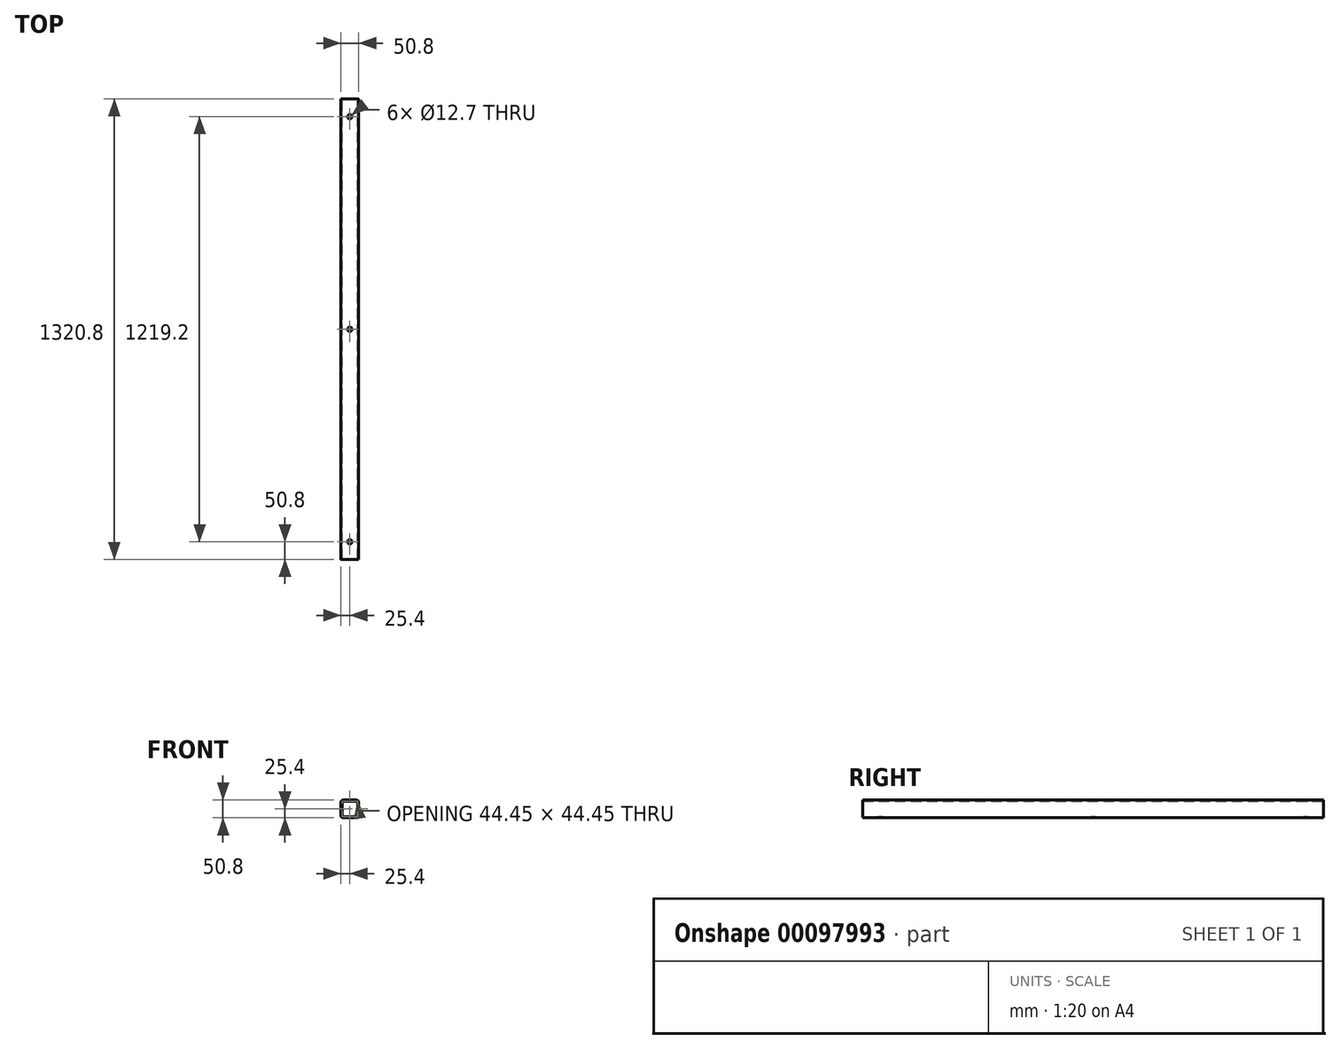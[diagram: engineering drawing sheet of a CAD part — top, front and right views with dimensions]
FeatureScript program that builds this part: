
annotation { "Feature Type Name" : "Feature", "Feature Type Description" : "" }
export const myFeature = defineFeature(function(context is Context, id is Id, definition is map)
    precondition{}
    {
        {
            var Q0;
            Q0=qCreatedBy(makeId("Front.planeOp"),FACE);
            var sketch = newSketch(context, id + "F0", { "sketchPlane" : qUnion([Q0])});
            skLineSegment(sketch, "E0.bottom", {"start": v(19.05, -25.4) * mm, "end": v(-19.05, -25.4) * mm});
            skLineSegment(sketch, "E0.top", {"start": v(19.05, 25.4) * mm, "end": v(-19.05, 25.4) * mm});
            skLineSegment(sketch, "E0.left", {"start": v(25.4, -19.05) * mm, "end": v(25.4, 19.05) * mm});
            skLineSegment(sketch, "E0.right", {"start": v(-25.4, -19.05) * mm, "end": v(-25.4, 19.05) * mm});
            skPoint(sketch, "E0.middle", {"position": v(0, 0) * mm});
            skLineSegment(sketch, "E1.bottom", {"start": v(19.05, 22.22) * mm, "end": v(-19.05, 22.22) * mm});
            skLineSegment(sketch, "E1.top", {"start": v(19.05, -22.23) * mm, "end": v(-19.05, -22.23) * mm});
            skLineSegment(sketch, "E1.left", {"start": v(22.22, 19.05) * mm, "end": v(22.22, -19.05) * mm});
            skLineSegment(sketch, "E1.right", {"start": v(-22.23, 19.05) * mm, "end": v(-22.23, -19.05) * mm});
            skPoint(sketch, "E2.visualSharp", {"position": v(-25.4, 25.4) * mm});
            skArc(sketch, "E2.filletArc", {"start": v(-19.05, 25.4) * mm, "mid": v(-23.54, 23.54) * mm, "end": v(-25.4, 19.05) * mm});
            skPoint(sketch, "E3.visualSharp", {"position": v(25.4, 25.4) * mm});
            skArc(sketch, "E3.filletArc", {"start": v(25.4, 19.05) * mm, "mid": v(23.54, 23.54) * mm, "end": v(19.05, 25.4) * mm});
            skPoint(sketch, "E4.visualSharp", {"position": v(25.4, -25.4) * mm});
            skArc(sketch, "E4.filletArc", {"start": v(19.05, -25.4) * mm, "mid": v(23.54, -23.54) * mm, "end": v(25.4, -19.05) * mm});
            skPoint(sketch, "E5.visualSharp", {"position": v(-25.4, -25.4) * mm});
            skArc(sketch, "E5.filletArc", {"start": v(-25.4, -19.05) * mm, "mid": v(-23.54, -23.54) * mm, "end": v(-19.05, -25.4) * mm});
            skPoint(sketch, "E6.visualSharp", {"position": v(22.22, 22.22) * mm});
            skArc(sketch, "E6.filletArc", {"start": v(22.22, 19.05) * mm, "mid": v(21.3, 21.3) * mm, "end": v(19.05, 22.22) * mm});
            skPoint(sketch, "E7.visualSharp", {"position": v(22.22, -22.23) * mm});
            skArc(sketch, "E7.filletArc", {"start": v(19.05, -22.23) * mm, "mid": v(21.3, -21.3) * mm, "end": v(22.22, -19.05) * mm});
            skPoint(sketch, "E8.visualSharp", {"position": v(-22.23, -22.23) * mm});
            skArc(sketch, "E8.filletArc", {"start": v(-22.22, -19.05) * mm, "mid": v(-21.3, -21.3) * mm, "end": v(-19.05, -22.23) * mm});
            skPoint(sketch, "E9.visualSharp", {"position": v(-22.23, 22.22) * mm});
            skArc(sketch, "E9.filletArc", {"start": v(-19.05, 22.22) * mm, "mid": v(-21.3, 21.3) * mm, "end": v(-22.22, 19.05) * mm});
            skSolve(sketch);
        }
        {
            var Q0;
            Q0=makeQuery(id+"F0.imprint","IMPRINT",FACE,{"disambiguationData":[TD([[makeQuery(id+"F0.imprint","IMPRINT",EDGE,{"derivedFrom":sQuery(id+"F0.wireOp",EDGE,"E0.bottom")}),-1.0]])]});
            extrude(context, id + "F1", {"entities" : qUnion([Q0]), "endBound" : BoundingType.SYMMETRIC, "depth" : 1320.8 * mm});
        }
        {
            var Q0;
            Q0=makeQuery(id+"F1.opExtrude","SWEPT_FACE",FACE,{"disambiguationData":[OSD([sQuery(id+"F0.wireOp",EDGE,"E0.top")])]});
            var sketch = newSketch(context, id + "F2", { "sketchPlane" : qUnion([Q0])});
            skCircle(sketch, "E10", {"center": v(0, 0) * mm, "radius": 6.35 * mm});
            skLineSegment(sketch, "E11", {"start": v(0, 776.87) * mm, "end": v(0, -912.17) * mm, "construction": true});
            skPoint(sketch, "E11.startSnap0", {"position": v(0, 660.4) * mm});
            skLineSegment(sketch, "E12", {"start": v(-122.07, 609.6) * mm, "end": v(132.48, 609.6) * mm, "construction": true});
            skCircle(sketch, "E13", {"center": v(0, 609.6) * mm, "radius": 6.35 * mm});
            skLineSegment(sketch, "E14", {"start": v(-93.72, -609.6) * mm, "end": v(85.54, -609.6) * mm, "construction": true});
            skCircle(sketch, "E15", {"center": v(0, -609.6) * mm, "radius": 6.35 * mm});
            skSolve(sketch);
        }
        {
            var Q0;
            Q0=makeQuery(id+"F2.imprint","IMPRINT",FACE,{"disambiguationData":[TD([[makeQuery(id+"F2.imprint","IMPRINT",EDGE,{"derivedFrom":sQuery(id+"F2.wireOp",EDGE,"E10")}),1.0]])]});
            var Q1;
            Q1=makeQuery(id+"F2.imprint","IMPRINT",FACE,{"disambiguationData":[TD([[makeQuery(id+"F2.imprint","IMPRINT",EDGE,{"derivedFrom":sQuery(id+"F2.wireOp",EDGE,"E15")}),1.0]])]});
            var Q2;
            Q2=makeQuery(id+"F2.imprint","IMPRINT",FACE,{"disambiguationData":[TD([[makeQuery(id+"F2.imprint","IMPRINT",EDGE,{"derivedFrom":sQuery(id+"F2.wireOp",EDGE,"E13")}),1.0]])]});
            extrude(context, id + "F3", {"entities" : qUnion([Q0, Q1, Q2]), "operationType" : NewBodyOperationType.REMOVE, "endBound" : BoundingType.THROUGH_ALL, "oppositeDirection" : true, "depth" : 25.4 * mm});
        }
    });
